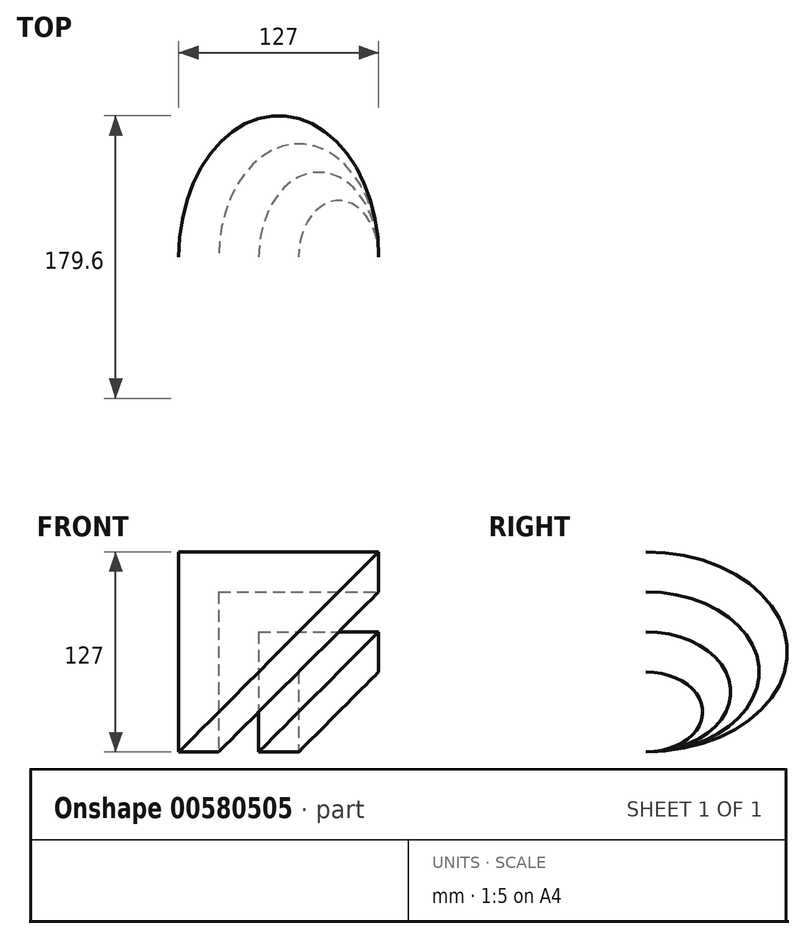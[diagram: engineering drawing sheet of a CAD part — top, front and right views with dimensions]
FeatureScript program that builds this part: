
annotation { "Feature Type Name" : "Feature", "Feature Type Description" : "" }
export const myFeature = defineFeature(function(context is Context, id is Id, definition is map)
    precondition{}
    {
        {
            var Q0;
            Q0=qCreatedBy(makeId("Front.planeOp"),FACE);
            var sketch = newSketch(context, id + "F0", { "sketchPlane" : qUnion([Q0])});
            skLineSegment(sketch, "E0", {"start": v(-66.54, 41.37) * mm, "end": v(60.46, 41.37) * mm});
            skLineSegment(sketch, "E1", {"start": v(-66.54, 15.97) * mm, "end": v(60.46, 15.97) * mm});
            skLineSegment(sketch, "E2", {"start": v(-66.54, -9.43) * mm, "end": v(60.46, -9.43) * mm});
            skLineSegment(sketch, "E3", {"start": v(-66.54, -34.83) * mm, "end": v(60.46, -34.83) * mm});
            skLineSegment(sketch, "E4", {"start": v(-66.54, 66.77) * mm, "end": v(60.46, 66.77) * mm});
            skLineSegment(sketch, "E5", {"start": v(-66.54, 92.17) * mm, "end": v(60.46, 92.17) * mm});
            skLineSegment(sketch, "E6", {"start": v(-66.54, 92.17) * mm, "end": v(60.46, -34.83) * mm});
            skLineSegment(sketch, "E7", {"start": v(60.46, 92.17) * mm, "end": v(60.46, -34.83) * mm});
            skLineSegment(sketch, "E8", {"start": v(-66.54, -34.83) * mm, "end": v(-66.54, 92.17) * mm});
            skSolve(sketch);
        }
        {
            var Q0;
            {var subQ0=sQuery(id+"F0.wireOp",EDGE,"E7");var subQ1=sQuery(id+"F0.wireOp",EDGE,"E0");var subQ2=makeQuery(id+"F0.imprint","INTERSECT",VERTEX,{"derivedFrom":[subQ1,subQ0]});Q0=makeQuery(id+"F0.imprint","IMPRINT",FACE,{"disambiguationData":[TD([[makeQuery(id+"F0.imprint","IMPRINT",EDGE,{"disambiguationData":[TD([[subQ2,1.0]])],"derivedFrom":subQ1}),-1.0]])]});}
            var Q1;
            {var subQ0=sQuery(id+"F0.wireOp",EDGE,"E8");var subQ1=sQuery(id+"F0.wireOp",EDGE,"E1");var subQ2=makeQuery(id+"F0.imprint","INTERSECT",VERTEX,{"derivedFrom":[subQ1,subQ0]});Q1=makeQuery(id+"F0.imprint","IMPRINT",FACE,{"disambiguationData":[TD([[makeQuery(id+"F0.imprint","IMPRINT",EDGE,{"disambiguationData":[TD([[subQ2,-1.0]])],"derivedFrom":subQ1}),-1.0]])]});}
            var Q2;
            {var subQ5=sQuery(id+"F0.wireOp",EDGE,"E5");Q2=makeQuery(id+"F0.imprint","IMPRINT",FACE,{"disambiguationData":[TD([[makeQuery(id+"F0.imprint","IMPRINT",EDGE,{"derivedFrom":subQ5}),-1.0]])]});}
            var Q3;
            Q3=sQuery(id+"F0.wireOp",EDGE,"E6");
            revolve(context, id + "F1", {"entities" : qUnion([Q0, Q1, Q2]), "axis" : qUnion([Q3]), "revolveType" : RevolveType.FULL});
        }
        {
            var Q0;
            Q0=makeQuery(id+"F1.opRevolve","SWEPT_BODY",BODY,{"disambiguationData":[OSD([sQuery(id+"F0.wireOp",EDGE,"E4"),sQuery(id+"F0.wireOp",EDGE,"E5"),sQuery(id+"F0.wireOp",EDGE,"E6"),sQuery(id+"F0.wireOp",EDGE,"E7")])]});
            var Q1;
            Q1=makeQuery(id+"F1.opRevolve","SWEPT_BODY",BODY,{"disambiguationData":[OSD([sQuery(id+"F0.wireOp",EDGE,"E1"),sQuery(id+"F0.wireOp",EDGE,"E2"),sQuery(id+"F0.wireOp",EDGE,"E6"),sQuery(id+"F0.wireOp",EDGE,"E8")])]});
            booleanBodies(context, id + "F2", {"operationType" : BooleanOperationType.SUBTRACTION, "tools" : qUnion([Q0]), "targets" : qUnion([Q1]), "keepTools" : true});
        }
        {
            var Q0;
            Q0=makeQuery(id+"F1.opRevolve","SWEPT_BODY",BODY,{"disambiguationData":[OSD([sQuery(id+"F0.wireOp",EDGE,"E0"),sQuery(id+"F0.wireOp",EDGE,"E1"),sQuery(id+"F0.wireOp",EDGE,"E6"),sQuery(id+"F0.wireOp",EDGE,"E7")])]});
            var Q1;
            Q1=makeQuery(id+"F1.opRevolve","SWEPT_BODY",BODY,{"disambiguationData":[OSD([sQuery(id+"F0.wireOp",EDGE,"E1"),sQuery(id+"F0.wireOp",EDGE,"E2"),sQuery(id+"F0.wireOp",EDGE,"E6"),sQuery(id+"F0.wireOp",EDGE,"E8")])]});
            booleanBodies(context, id + "F3", {"operationType" : BooleanOperationType.SUBTRACTION, "tools" : qUnion([Q0]), "targets" : qUnion([Q1]), "keepTools" : true});
        }
        {
            var Q0;
            Q0=makeQuery(id+"F3.opBoolean","SPLIT",BODY,{"disambiguationData":[OD(1.0)],"derivedFrom":makeQuery(id+"F1.opRevolve","SWEPT_BODY",BODY,{"disambiguationData":[OSD([sQuery(id+"F0.wireOp",EDGE,"E1"),sQuery(id+"F0.wireOp",EDGE,"E2"),sQuery(id+"F0.wireOp",EDGE,"E6"),sQuery(id+"F0.wireOp",EDGE,"E8")])]})});
            deleteBodies(context, id + "F4", {"entities" : qUnion([Q0])});
        }
    });
